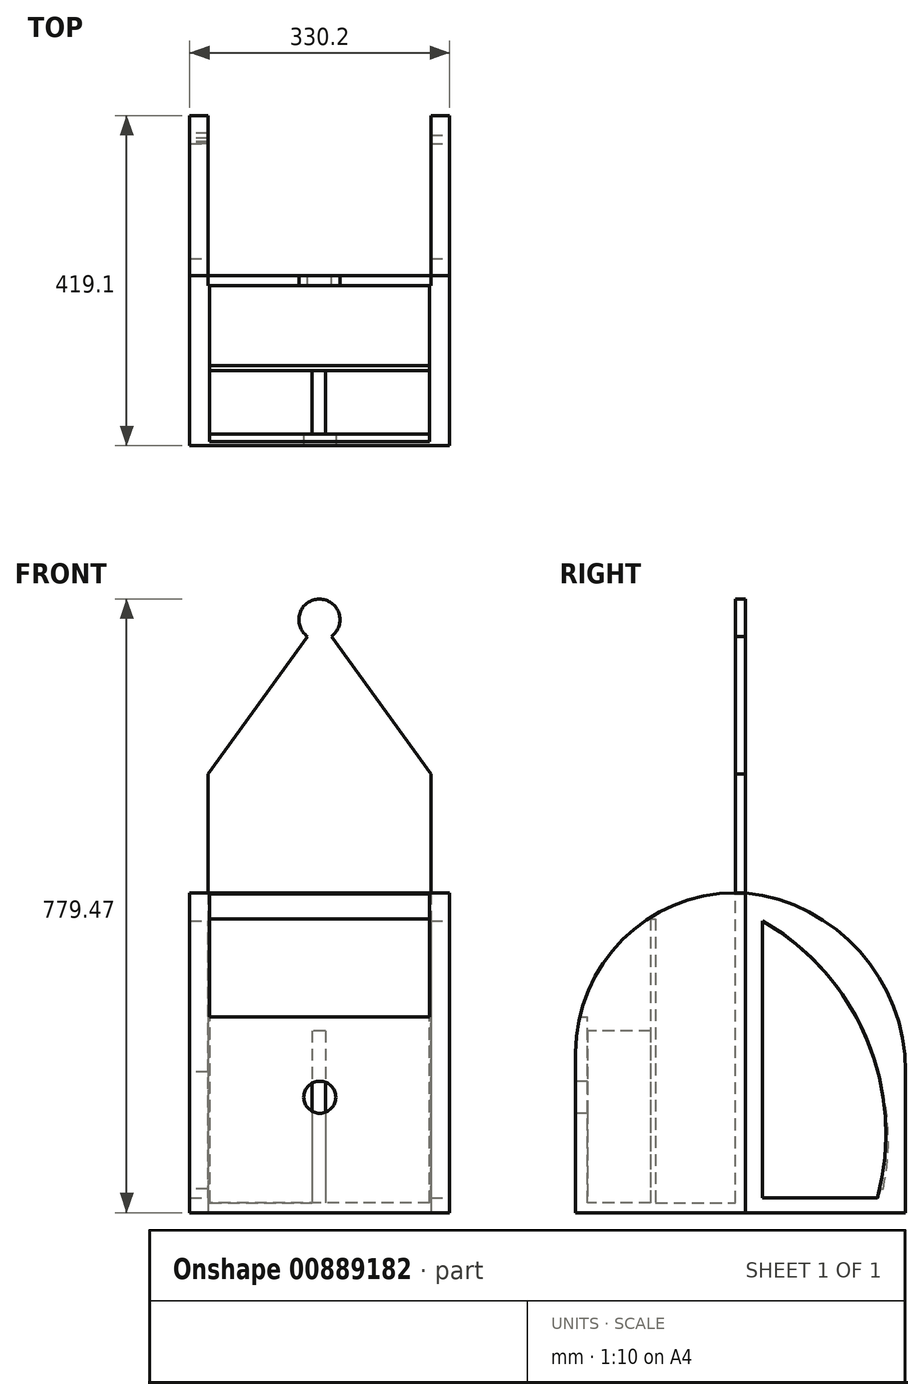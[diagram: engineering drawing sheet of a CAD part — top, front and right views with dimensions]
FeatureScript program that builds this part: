
annotation { "Feature Type Name" : "Feature", "Feature Type Description" : "" }
export const myFeature = defineFeature(function(context is Context, id is Id, definition is map)
    precondition{}
    {
        {
            var Q0;
            Q0=qCreatedBy(makeId("Front.planeOp"),FACE);
            var sketch = newSketch(context, id + "F0", { "sketchPlane" : qUnion([Q0])});
            skLineSegment(sketch, "E0.bottom", {"start": v(-116.84, 203.2) * mm, "end": v(-447.04, 203.2) * mm});
            skLineSegment(sketch, "E0.top", {"start": v(-116.84, -203.2) * mm, "end": v(-447.04, -203.2) * mm});
            skLineSegment(sketch, "E0.left", {"start": v(-116.84, 203.2) * mm, "end": v(-116.84, -203.2) * mm});
            skLineSegment(sketch, "E0.right", {"start": v(-447.04, 203.2) * mm, "end": v(-447.04, -203.2) * mm});
            skPoint(sketch, "E0.middle", {"position": v(0, 0) * mm});
            skSolve(sketch);
        }
        {
            var Q0;
            Q0=makeQuery(id+"F0.imprint","IMPRINT",FACE,{"disambiguationData":[TD([[makeQuery(id+"F0.imprint","IMPRINT",EDGE,{"derivedFrom":sQuery(id+"F0.wireOp",EDGE,"E0.bottom")}),1.0]])]});
            extrude(context, id + "F1", {"entities" : qUnion([Q0]), "depth" : 12.7 * mm, "offsetDistance" : 25.4 * mm});
        }
        {
            var Q0;
            Q0=makeQuery(id+"F1.opExtrude","CAP_FACE",FACE,{"disambiguationData":[OSD([sQuery(id+"F0.wireOp",EDGE,"E0.bottom"),sQuery(id+"F0.wireOp",EDGE,"E0.top"),sQuery(id+"F0.wireOp",EDGE,"E0.left"),sQuery(id+"F0.wireOp",EDGE,"E0.right")])],"isStart":false});
            var sketch = newSketch(context, id + "F2", { "sketchPlane" : qUnion([Q0])});
            skLineSegment(sketch, "E1.bottom", {"start": v(-447.04, -203.2) * mm, "end": v(-421.64, -203.2) * mm});
            skLineSegment(sketch, "E1.top", {"start": v(-447.04, -177.8) * mm, "end": v(-421.64, -177.8) * mm});
            skLineSegment(sketch, "E1.left", {"start": v(-447.04, -203.2) * mm, "end": v(-447.04, -177.8) * mm});
            skLineSegment(sketch, "E1.right", {"start": v(-421.64, -203.2) * mm, "end": v(-421.64, -177.8) * mm});
            skLineSegment(sketch, "E2.bottom", {"start": v(-116.84, -203.2) * mm, "end": v(-142.24, -203.2) * mm});
            skLineSegment(sketch, "E2.top", {"start": v(-116.84, -177.8) * mm, "end": v(-142.24, -177.8) * mm});
            skLineSegment(sketch, "E2.left", {"start": v(-116.84, -203.2) * mm, "end": v(-116.84, -177.8) * mm});
            skLineSegment(sketch, "E2.right", {"start": v(-142.24, -203.2) * mm, "end": v(-142.24, -177.8) * mm});
            skSolve(sketch);
        }
        {
            var Q0;
            Q0=makeQuery(id+"F2.imprint","IMPRINT",FACE,{"disambiguationData":[TD([[makeQuery(id+"F2.imprint","IMPRINT",EDGE,{"derivedFrom":sQuery(id+"F2.wireOp",EDGE,"E1.bottom")}),-1.0]])]});
            var Q1;
            Q1=makeQuery(id+"F2.imprint","IMPRINT",FACE,{"disambiguationData":[TD([[makeQuery(id+"F2.imprint","IMPRINT",EDGE,{"derivedFrom":sQuery(id+"F2.wireOp",EDGE,"E2.bottom")}),-1.0]])]});
            extrude(context, id + "F3", {"entities" : qUnion([Q0, Q1]), "operationType" : NewBodyOperationType.ADD, "depth" : 203.2 * mm, "offsetDistance" : 25.4 * mm});
        }
        {
            var Q0;
            Q0=makeQuery(id+"F1.opExtrude","CAP_FACE",FACE,{"disambiguationData":[OSD([sQuery(id+"F0.wireOp",EDGE,"E0.bottom"),sQuery(id+"F0.wireOp",EDGE,"E0.top"),sQuery(id+"F0.wireOp",EDGE,"E0.left"),sQuery(id+"F0.wireOp",EDGE,"E0.right")])],"isStart":false});
            var sketch = newSketch(context, id + "F4", { "sketchPlane" : qUnion([Q0])});
            skLineSegment(sketch, "E3.bottom", {"start": v(-116.84, 203.2) * mm, "end": v(-142.24, 203.2) * mm});
            skLineSegment(sketch, "E3.top", {"start": v(-116.84, -177.8) * mm, "end": v(-142.24, -177.8) * mm});
            skLineSegment(sketch, "E3.left", {"start": v(-116.84, 203.2) * mm, "end": v(-116.84, -177.8) * mm});
            skLineSegment(sketch, "E3.right", {"start": v(-142.24, 203.2) * mm, "end": v(-142.24, -177.8) * mm});
            skLineSegment(sketch, "E4.bottom", {"start": v(-447.04, 203.2) * mm, "end": v(-421.64, 203.2) * mm});
            skLineSegment(sketch, "E4.top", {"start": v(-447.04, -177.8) * mm, "end": v(-421.64, -177.8) * mm});
            skLineSegment(sketch, "E4.left", {"start": v(-447.04, 203.2) * mm, "end": v(-447.04, -177.8) * mm});
            skLineSegment(sketch, "E4.right", {"start": v(-421.64, 203.2) * mm, "end": v(-421.64, -177.8) * mm});
            skSolve(sketch);
        }
        {
            var Q0;
            Q0=makeQuery(id+"F4.imprint","IMPRINT",FACE,{"disambiguationData":[TD([[makeQuery(id+"F4.imprint","IMPRINT",EDGE,{"derivedFrom":sQuery(id+"F4.wireOp",EDGE,"E4.bottom")}),1.0]])]});
            var Q1;
            Q1=makeQuery(id+"F4.imprint","IMPRINT",FACE,{"disambiguationData":[TD([[makeQuery(id+"F4.imprint","IMPRINT",EDGE,{"derivedFrom":sQuery(id+"F4.wireOp",EDGE,"E3.bottom")}),1.0]])]});
            extrude(context, id + "F5", {"entities" : qUnion([Q0, Q1]), "operationType" : NewBodyOperationType.ADD, "depth" : 203.2 * mm, "offsetDistance" : 25.4 * mm});
        }
        {
            var Q0;
            Q0=makeQuery(id+"F5.opExtrude","CAP_EDGE",EDGE,{"disambiguationData":[OSD([sQuery(id+"F4.wireOp",EDGE,"E4.bottom")])],"isStart":false});
            var Q1;
            Q1=makeQuery(id+"F5.opExtrude","CAP_EDGE",EDGE,{"disambiguationData":[OSD([sQuery(id+"F4.wireOp",EDGE,"E3.bottom")])],"isStart":false});
            fillet(context, id + "F6", {"entities" : qUnion([Q0, Q1]), "radius" : 203.2 * mm, "tangentPropagation" : true, "allowEdgeOverflow" : false});
        }
        {
            var Q0;
            Q0=makeQuery(id+"FgqJypWpbvrxkFR_1.boolean.opBoolean","MERGE",FACE,{"derivedFrom":[makeQuery(id+"F3.boolean.opBoolean","MERGE",FACE,{"derivedFrom":[makeQuery(id+"F1.opExtrude","SWEPT_FACE",FACE,{"disambiguationData":[OSD([sQuery(id+"F0.wireOp",EDGE,"E0.top")])]}),makeQuery(id+"F3.opExtrude","SWEPT_FACE",FACE,{"disambiguationData":[OSD([sQuery(id+"F2.wireOp",EDGE,"E1.bottom")])]}),makeQuery(id+"F3.opExtrude","SWEPT_FACE",FACE,{"disambiguationData":[OSD([sQuery(id+"F2.wireOp",EDGE,"E2.bottom")])]})]}),makeQuery(id+"FgqJypWpbvrxkFR_1.opExtrude","SWEPT_FACE",FACE,{"disambiguationData":[OSD([sQuery(id+"FrXqKcjXizDg0TU_1.wireOp",EDGE,"8OnaD963-bGuW-84mX-I4wE-5KUWDyE7E92f.bottom")])]})]});
            var sketch = newSketch(context, id + "F7", { "sketchPlane" : qUnion([Q0])});
            skLineSegment(sketch, "E5.bottom", {"start": v(-447.04, 215.9) * mm, "end": v(-116.84, 215.9) * mm});
            skLineSegment(sketch, "E5.top", {"start": v(-447.04, 0) * mm, "end": v(-116.84, 0) * mm});
            skLineSegment(sketch, "E5.left", {"start": v(-447.04, 215.9) * mm, "end": v(-447.04, 0) * mm});
            skLineSegment(sketch, "E5.right", {"start": v(-116.84, 215.9) * mm, "end": v(-116.84, 0) * mm});
            skSolve(sketch);
        }
        {
            var Q0;
            {var subQ0=sQuery(id+"F0.wireOp",EDGE,"E0.top");Q0=makeQuery(id+"F7.imprint","IMPRINT",FACE,{"disambiguationData":[TD([[makeQuery(id+"F7.imprint","IMPRINT",EDGE,{"derivedFrom":makeQuery(id+"F1.opExtrude","CAP_EDGE",EDGE,{"disambiguationData":[OSD([subQ0])],"isStart":false})}),-1.0]])]});}
            extrude(context, id + "F8", {"entities" : qUnion([Q0]), "oppositeDirection" : true, "depth" : 12.7 * mm, "offsetDistance" : 25.4 * mm});
        }
        {
            var Q0;
            Q0=makeQuery(id+"F5.boolean.opBoolean","MERGE",FACE,{"derivedFrom":[makeQuery(id+"F3.opExtrude","SWEPT_FACE",FACE,{"disambiguationData":[OSD([sQuery(id+"F2.wireOp",EDGE,"E1.right")])]}),makeQuery(id+"F5.opExtrude","SWEPT_FACE",FACE,{"disambiguationData":[OSD([sQuery(id+"F4.wireOp",EDGE,"E4.right")])]})]});
            var sketch = newSketch(context, id + "F9", { "sketchPlane" : qUnion([Q0])});
            skLineSegment(sketch, "E6.bottom", {"start": v(-215.9, -190.5) * mm, "end": v(-201.05, -190.5) * mm});
            skLineSegment(sketch, "E6.top", {"start": v(-215.9, 45.46) * mm, "end": v(-201.05, 45.46) * mm});
            skLineSegment(sketch, "E6.left", {"start": v(-215.9, -190.5) * mm, "end": v(-215.9, 45.46) * mm});
            skLineSegment(sketch, "E6.right", {"start": v(-201.05, -190.5) * mm, "end": v(-201.05, 45.46) * mm});
            skSolve(sketch);
        }
        {
            var Q0;
            {var subQ3=sQuery(id+"F9.wireOp",EDGE,"E6.bottom");Q0=makeQuery(id+"F9.imprint","IMPRINT",FACE,{"disambiguationData":[TD([[makeQuery(id+"F9.imprint","IMPRINT",EDGE,{"derivedFrom":subQ3}),1.0]])]});}
            extrude(context, id + "F10", {"entities" : qUnion([Q0]), "operationType" : NewBodyOperationType.ADD, "depth" : 279.4 * mm, "offsetDistance" : 25.4 * mm});
        }
        {
            var Q0;
            Q0=qCreatedBy(makeId("Front.planeOp"),FACE);
            var sketch = newSketch(context, id + "F11", { "sketchPlane" : qUnion([Q0])});
            skLineSegment(sketch, "E7.bottom", {"start": v(-423.97, 201.8) * mm, "end": v(-140.92, 201.8) * mm});
            skLineSegment(sketch, "E7.left", {"start": v(-423.97, 201.8) * mm, "end": v(-423.97, 354.2) * mm});
            skLineSegment(sketch, "E7.right", {"start": v(-140.92, 201.8) * mm, "end": v(-140.92, 354.2) * mm});
            skLineSegment(sketch, "E8", {"start": v(-423.97, 354.2) * mm, "end": v(-297.75, 528.93) * mm});
            skLineSegment(sketch, "E9", {"start": v(-267.13, 528.93) * mm, "end": v(-140.92, 354.2) * mm});
            skPoint(sketch, "E10.start.orphan", {"position": v(-282.44, 201.8) * mm});
            skArc(sketch, "E11", {"start": v(-267.13, 528.93) * mm, "mid": v(-282.44, 576.27) * mm, "end": v(-297.75, 528.93) * mm});
            skSolve(sketch);
        }
        {
            var Q0;
            Q0=makeQuery(id+"F11.imprint","IMPRINT",FACE,{"disambiguationData":[TD([[makeQuery(id+"F11.imprint","IMPRINT",EDGE,{"derivedFrom":sQuery(id+"F11.wireOp",EDGE,"E7.bottom")}),1.0]])]});
            extrude(context, id + "F12", {"entities" : qUnion([Q0]), "depth" : 12.7 * mm, "offsetDistance" : 25.4 * mm});
        }
        {
            var Q0;
            Q0=makeQuery(id+"F10.boolean.opBoolean","MERGE",FACE,{"derivedFrom":[makeQuery(id+"F8.boolean.opBoolean","MERGE",FACE,{"derivedFrom":[makeQuery(id+"F5.boolean.opBoolean","MERGE",FACE,{"derivedFrom":[makeQuery(id+"F3.opExtrude","CAP_FACE",FACE,{"disambiguationData":[OSD([sQuery(id+"F2.wireOp",EDGE,"E1.bottom"),sQuery(id+"F2.wireOp",EDGE,"E1.top"),sQuery(id+"F2.wireOp",EDGE,"E1.left"),sQuery(id+"F2.wireOp",EDGE,"E1.right")])],"isStart":false}),makeQuery(id+"F5.opExtrude","CAP_FACE",FACE,{"disambiguationData":[OSD([sQuery(id+"F4.wireOp",EDGE,"E4.bottom"),sQuery(id+"F4.wireOp",EDGE,"E4.top"),sQuery(id+"F4.wireOp",EDGE,"E4.left"),sQuery(id+"F4.wireOp",EDGE,"E4.right")])],"isStart":false})]}),makeQuery(id+"F5.boolean.opBoolean","MERGE",FACE,{"derivedFrom":[makeQuery(id+"F3.opExtrude","CAP_FACE",FACE,{"disambiguationData":[OSD([sQuery(id+"F2.wireOp",EDGE,"E2.bottom"),sQuery(id+"F2.wireOp",EDGE,"E2.top"),sQuery(id+"F2.wireOp",EDGE,"E2.left"),sQuery(id+"F2.wireOp",EDGE,"E2.right")])],"isStart":false}),makeQuery(id+"F5.opExtrude","CAP_FACE",FACE,{"disambiguationData":[OSD([sQuery(id+"F4.wireOp",EDGE,"E3.bottom"),sQuery(id+"F4.wireOp",EDGE,"E3.top"),sQuery(id+"F4.wireOp",EDGE,"E3.left"),sQuery(id+"F4.wireOp",EDGE,"E3.right")])],"isStart":false})]}),makeQuery(id+"F8.opExtrude","SWEPT_FACE",FACE,{"disambiguationData":[OSD([sQuery(id+"F7.wireOp",EDGE,"E5.bottom")])]})]}),makeQuery(id+"F10.opExtrude","SWEPT_FACE",FACE,{"disambiguationData":[OSD([sQuery(id+"F9.wireOp",EDGE,"E6.left")])]})]});
            var sketch = newSketch(context, id + "F13", { "sketchPlane" : qUnion([Q0])});
            skCircle(sketch, "E12", {"center": v(-281.94, -56.56) * mm, "radius": 20.37 * mm});
            skPoint(sketch, "E12.centerSnap0", {"position": v(-281.94, 0) * mm});
            skSolve(sketch);
        }
        {
            var Q0;
            Q0=makeQuery(id+"F13.imprint","IMPRINT",FACE,{"disambiguationData":[TD([[makeQuery(id+"F13.imprint","IMPRINT",EDGE,{"derivedFrom":sQuery(id+"F13.wireOp",EDGE,"E12")}),1.0]])]});
            extrude(context, id + "F14", {"entities" : qUnion([Q0]), "operationType" : NewBodyOperationType.REMOVE, "oppositeDirection" : true, "depth" : 25.4 * mm, "offsetDistance" : 25.4 * mm});
        }
        {
            var Q0;
            Q0=makeQuery(id+"F12.boolean.opBoolean","MERGE",FACE,{"derivedFrom":[makeQuery(id+"F1.opExtrude","CAP_FACE",FACE,{"disambiguationData":[OSD([sQuery(id+"F0.wireOp",EDGE,"E0.bottom"),sQuery(id+"F0.wireOp",EDGE,"E0.top"),sQuery(id+"F0.wireOp",EDGE,"E0.left"),sQuery(id+"F0.wireOp",EDGE,"E0.right")])],"isStart":true}),makeQuery(id+"F12.opExtrude","CAP_FACE",FACE,{"disambiguationData":[OSD([sQuery(id+"F11.wireOp",EDGE,"E7.bottom"),sQuery(id+"F11.wireOp",EDGE,"E7.left"),sQuery(id+"F11.wireOp",EDGE,"E7.right"),sQuery(id+"F11.wireOp",EDGE,"E8"),sQuery(id+"F11.wireOp",EDGE,"E9"),sQuery(id+"F11.wireOp",EDGE,"E11")])],"isStart":true})]});
            var sketch = newSketch(context, id + "F15", { "sketchPlane" : qUnion([Q0])});
            skLineSegment(sketch, "E13.bottom", {"start": v(116.84, 203.2) * mm, "end": v(140.92, 203.2) * mm});
            skLineSegment(sketch, "E13.top", {"start": v(116.84, -203.2) * mm, "end": v(140.92, -203.2) * mm});
            skLineSegment(sketch, "E13.left", {"start": v(116.84, 203.2) * mm, "end": v(116.84, -203.2) * mm});
            skLineSegment(sketch, "E13.right", {"start": v(140.92, 203.2) * mm, "end": v(140.92, -203.2) * mm});
            skLineSegment(sketch, "E14.bottom", {"start": v(423.97, 203.2) * mm, "end": v(447.04, 203.2) * mm});
            skLineSegment(sketch, "E14.top", {"start": v(423.97, -203.2) * mm, "end": v(447.04, -203.2) * mm});
            skLineSegment(sketch, "E14.left", {"start": v(423.97, 203.2) * mm, "end": v(423.97, -203.2) * mm});
            skLineSegment(sketch, "E14.right", {"start": v(447.04, 203.2) * mm, "end": v(447.04, -203.2) * mm});
            skSolve(sketch);
        }
        {
            var Q0;
            Q0 = qSketchRegion(id + "F15", true);
            extrude(context, id + "F16", {"entities" : qUnion([Q0]), "depth" : 203.2 * mm, "offsetDistance" : 25.4 * mm});
        }
        {
            var Q0;
            Q0=makeQuery(id+"F16.opExtrude","CAP_EDGE",EDGE,{"disambiguationData":[OSD([sQuery(id+"F15.wireOp",EDGE,"E13.bottom")])],"isStart":false});
            var Q1;
            Q1=makeQuery(id+"F16.opExtrude","CAP_EDGE",EDGE,{"disambiguationData":[OSD([sQuery(id+"F15.wireOp",EDGE,"E14.bottom")])],"isStart":false});
            fillet(context, id + "F17", {"entities" : qUnion([Q0, Q1]), "radius" : 228.6 * mm, "tangentPropagation" : true, "allowEdgeOverflow" : false});
        }
        {
            var Q0;
            Q0=makeQuery(id+"F16.boolean.opBoolean","MERGE",FACE,{"derivedFrom":[makeQuery(id+"F5.boolean.opBoolean","MERGE",FACE,{"derivedFrom":[makeQuery(id+"F3.boolean.opBoolean","MERGE",FACE,{"derivedFrom":[makeQuery(id+"F1.opExtrude","SWEPT_FACE",FACE,{"disambiguationData":[OSD([sQuery(id+"F0.wireOp",EDGE,"E0.left")])]}),makeQuery(id+"F3.opExtrude","SWEPT_FACE",FACE,{"disambiguationData":[OSD([sQuery(id+"F2.wireOp",EDGE,"E2.left")])]})]}),makeQuery(id+"F5.opExtrude","SWEPT_FACE",FACE,{"disambiguationData":[OSD([sQuery(id+"F4.wireOp",EDGE,"E3.left")])]})]}),makeQuery(id+"F16.opExtrude","SWEPT_FACE",FACE,{"disambiguationData":[OSD([sQuery(id+"F15.wireOp",EDGE,"E13.left")])]})]});
            var sketch = newSketch(context, id + "F18", { "sketchPlane" : qUnion([Q0])});
            skLineSegment(sketch, "E15", {"start": v(21.42, 167.54) * mm, "end": v(21.42, -184.2) * mm});
            skLineSegment(sketch, "E16", {"start": v(21.42, -184.2) * mm, "end": v(167.57, -184.2) * mm});
            skArc(sketch, "E17", {"start": v(167.57, -184.2) * mm, "mid": v(154.2, 16.47) * mm, "end": v(21.42, 167.54) * mm});
            skSolve(sketch);
        }
        {
            var Q0;
            Q0=makeQuery(id+"F18.imprint","IMPRINT",FACE,{"disambiguationData":[TD([[makeQuery(id+"F18.imprint","IMPRINT",EDGE,{"derivedFrom":sQuery(id+"F18.wireOp",EDGE,"E15")}),1.0]])]});
            extrude(context, id + "F19", {"entities" : qUnion([Q0]), "operationType" : NewBodyOperationType.REMOVE, "oppositeDirection" : true, "depth" : 342.9 * mm, "offsetDistance" : 25.4 * mm});
        }
        {
            var Q0;
            Q0=makeQuery(id+"F8.opExtrude","CAP_FACE",FACE,{"disambiguationData":[OSD([sQuery(id+"F0.wireOp",EDGE,"E0.top"),sQuery(id+"F2.wireOp",EDGE,"E1.bottom"),sQuery(id+"F2.wireOp",EDGE,"E1.right"),sQuery(id+"F2.wireOp",EDGE,"E2.bottom"),sQuery(id+"F2.wireOp",EDGE,"E2.right"),sQuery(id+"F7.wireOp",EDGE,"E5.bottom")])],"isStart":false});
            var sketch = newSketch(context, id + "F20", { "sketchPlane" : qUnion([Q0])});
            skLineSegment(sketch, "E18.bottom", {"start": v(-421.64, -114.3) * mm, "end": v(-142.24, -114.3) * mm});
            skLineSegment(sketch, "E18.top", {"start": v(-421.64, -120.82) * mm, "end": v(-142.24, -120.82) * mm});
            skLineSegment(sketch, "E18.left", {"start": v(-421.64, -114.3) * mm, "end": v(-421.64, -120.82) * mm});
            skLineSegment(sketch, "E18.right", {"start": v(-142.24, -114.3) * mm, "end": v(-142.24, -120.82) * mm});
            skLineSegment(sketch, "E19.bottom", {"start": v(-281.94, -120.82) * mm, "end": v(-281.94, -120.82) * mm});
            skLineSegment(sketch, "E19.top", {"start": v(-281.94, -201.05) * mm, "end": v(-281.94, -201.05) * mm});
            skLineSegment(sketch, "E19.left", {"start": v(-281.94, -120.82) * mm, "end": v(-281.94, -201.05) * mm});
            skLineSegment(sketch, "E19.right", {"start": v(-281.94, -120.82) * mm, "end": v(-281.94, -201.05) * mm});
            skSolve(sketch);
        }
        {
            var Q0;
            Q0 = qSketchRegion(id + "F20", true);
            extrude(context, id + "F21", {"entities" : qUnion([Q0]), "operationType" : NewBodyOperationType.ADD, "depth" : 360.68 * mm, "offsetDistance" : 25.4 * mm});
        }
        {
            var Q0;
            {var subQ0=sQuery(id+"F2.wireOp",EDGE,"E2.right");var subQ1=sQuery(id+"F2.wireOp",EDGE,"E1.right");Q0=makeQuery(id+"F21.boolean.opBoolean","SPLIT",FACE,{"disambiguationData":[TD([makeQuery(id+"F10.opExtrude","SWEPT_FACE",FACE,{"disambiguationData":[OSD([sQuery(id+"F9.wireOp",EDGE,"E6.right")])]})])],"derivedFrom":makeQuery(id+"F8.opExtrude","CAP_FACE",FACE,{"disambiguationData":[OSD([sQuery(id+"F0.wireOp",EDGE,"E0.top"),sQuery(id+"F2.wireOp",EDGE,"E1.bottom"),subQ1,sQuery(id+"F2.wireOp",EDGE,"E2.bottom"),subQ0,sQuery(id+"F7.wireOp",EDGE,"E5.bottom")])],"isStart":false})});}
            var sketch = newSketch(context, id + "F22", { "sketchPlane" : qUnion([Q0])});
            skLineSegment(sketch, "E20.bottom", {"start": v(-291.5, -120.82) * mm, "end": v(-274.74, -120.82) * mm});
            skLineSegment(sketch, "E20.top", {"start": v(-291.5, -201.05) * mm, "end": v(-274.74, -201.05) * mm});
            skLineSegment(sketch, "E20.left", {"start": v(-291.5, -120.82) * mm, "end": v(-291.5, -201.05) * mm});
            skLineSegment(sketch, "E20.right", {"start": v(-274.74, -120.82) * mm, "end": v(-274.74, -201.05) * mm});
            skSolve(sketch);
        }
        {
            var Q0;
            Q0=makeQuery(id+"F22.imprint","IMPRINT",FACE,{"disambiguationData":[TD([[makeQuery(id+"F22.imprint","IMPRINT",EDGE,{"derivedFrom":sQuery(id+"F22.wireOp",EDGE,"E20.bottom")}),-1.0]])]});
            extrude(context, id + "F23", {"entities" : qUnion([Q0]), "operationType" : NewBodyOperationType.ADD, "depth" : 218.44 * mm, "offsetDistance" : 25.4 * mm});
        }
        {
            var Q0;
            Q0=makeQuery(id+"F16.opExtrude","SWEPT_FACE",FACE,{"disambiguationData":[OSD([sQuery(id+"F15.wireOp",EDGE,"E13.left")])]});
            var sketch = newSketch(context, id + "F24", { "sketchPlane" : qUnion([Q0])});
            skLineSegment(sketch, "E21", {"start": v(29.48, 151.74) * mm, "end": v(29.48, -173.35) * mm});
            skLineSegment(sketch, "E22", {"start": v(29.48, -173.35) * mm, "end": v(174.9, -173.35) * mm});
            skArc(sketch, "E23", {"start": v(174.9, -173.35) * mm, "mid": v(152.9, 11.88) * mm, "end": v(29.48, 151.74) * mm});
            skSolve(sketch);
        }
        {
            var Q0;
            Q0=makeQuery(id+"F24.imprint","IMPRINT",FACE,{"disambiguationData":[TD([[makeQuery(id+"F24.imprint","IMPRINT",EDGE,{"derivedFrom":sQuery(id+"F24.wireOp",EDGE,"E21")}),1.0]])]});
            extrude(context, id + "F25", {"entities" : qUnion([Q0]), "operationType" : NewBodyOperationType.REMOVE, "oppositeDirection" : true, "depth" : 355.6 * mm, "offsetDistance" : 25.4 * mm});
        }
        {
            var Q0;
            Q0=makeQuery(id+"F16.opExtrude","SWEPT_FACE",FACE,{"disambiguationData":[OSD([sQuery(id+"F15.wireOp",EDGE,"E14.right")])]});
            var sketch = newSketch(context, id + "F26", { "sketchPlane" : qUnion([Q0])});
            skLineSegment(sketch, "E24", {"start": v(-29.3, 151.62) * mm, "end": v(-29.3, -173) * mm});
            skLineSegment(sketch, "E25", {"start": v(-29.3, -173) * mm, "end": v(-174.72, -173) * mm});
            skArc(sketch, "E26", {"start": v(-22.67, 151.62) * mm, "mid": v(-152.9, 14.7) * mm, "end": v(-174.72, -173) * mm});
            skSolve(sketch);
        }
        {
            var Q0;
            {var subQ0=sQuery(id+"F26.wireOp",EDGE,"E25");Q0=makeQuery(id+"F26.imprint","IMPRINT",FACE,{"disambiguationData":[TD([[makeQuery(id+"F26.imprint","IMPRINT",EDGE,{"derivedFrom":subQ0}),-1.0]])]});}
            extrude(context, id + "F27", {"entities" : qUnion([Q0]), "operationType" : NewBodyOperationType.REMOVE, "oppositeDirection" : true, "depth" : 25.4 * mm, "offsetDistance" : 25.4 * mm});
        }
    });
